# Revit family: Sanitary_Toilets_TOTO-USA-Inc_NEORESTR-AH-Dual-Flush-Toilet-1-0-GPF-0
name_source: partatom
category: Plumbing Fixtures
revit_build: Autodesk Revit 2015 (Build: 20140606_1530(x64)
units: mm (PartAtom-declared; Revit-internal decimal feet)

## types (1)
- MS989CUMFG
    Ambient Temp. = 32F to 104F
    BIMobject category = Toilets
    BIMobject category code = sanitary-toilets
    BIMobject main category = Sanitary
    BIMobject main category code = sanitary
    Brand url = https://www.totousa.com
    Default Elevation = 4' - 0"
    Edition number = 1
    IFC Classification = Flow Terminal
    Manufacturer name = TOTO USA Inc
    Masterformat 2014 Code = 10 28 00
    Masterformat 2014 Description = Toilet, Bath, and Laundry Accessories
    Material = Galaline - TOTO - Reinforced Marble
    Material main = Ceramics
    Nominal height = 0' - 0"
    Nominal width = 0' - 0"
    OmniClass Code = 23-31 19 00
    OmniClass Description = Toilets
    Product Guid = d4826b34-5f6d-488a-b804-1bf6e174c4d6
    Product SKU = toto-ms989cumfg
    Product certification = https://www.totousa.com
    Product data url = https://bimobject.com
    Product family = Urinals
    Product group = NEOREST??
    Product url = https://www.totousa.com
    QR code = http://bimobject.com
    Rated Voltage = 120 V
    Rough-in = 1' - 0"
    Technical description = https://www.totousa.com
    Trap Seal = 0' - 2 1/8"
    Trap diameter = 0' - 2 1/8"
    UNSPSC Code = 30181505
    Uniclass 1.4 Code = L7216
    Uniclass 1.4 Description = Toilets
    Uniclass 2.0 Code = SS-35-65-90
    Uniclass 2.0 Description = Toilet Systems
    Uniclass 2015 Code = SL_35_80_89
    Uniclass 2015 Name = Toilets
    Uniformat II Code = D2030
    Uniformat II Description = Sanitary Waste
    Warranty = Three Year Limited(Residental), One Tear Limited(Commercial)
    Water Supply Pressure(Max) = 7.25 psi
    Water Supply Pressure(Min) = 108.75 psi

## geometry (parser evidence)
native form markers: Blend x4, Sweep x2
no freeform markers — native parametric forms only
